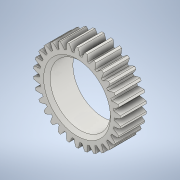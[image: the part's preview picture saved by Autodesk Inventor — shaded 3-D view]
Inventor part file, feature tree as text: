
AUTODESK INVENTOR PART (.ipt)
format: ipt  version: 2022 (Build 260153000, 153)  size: 621,568 bytes
history: native  units: mm (DEFAULTED — no unit token found)
features: plane x4, other x3, sketch x3, extrude x2, chamfer x1
ambient origin geometry x8: Origin, YZ Plane, XZ Plane, XY Plane, X Axis, Y Axis, Z Axis, Center Point
bodies: Solid1 (feature_tree)
feature tree (13):
  extrude  "Extrusion1"  Depth=9.525mm TaperAngle=0.0deg
  plane  "Work Plane1"
  plane  "Work Plane2"
  plane  "Work Plane3"
  other  "Spur Gear"
  extrude  "Extrusion2"  Depth=76.2mm TaperAngle=0.0deg
  plane  "Work Plane4"
  chamfer  "Chamfer1"  Distance=1.047198mm
  sketch  "Sketch1"  dims[d0=31.912126mm d1=9.525mm d2=0.0mm]
  sketch  "Sketch2"  dims[d3=30.0mm d4=76.2mm d5=0.0mm d6=0.0mm d7=1.047198mm]
  other  "Srf1"
  sketch  "Sketch3"  dims[d9=0.0mm d14=0.0mm d15=25.4mm d16=0.0mm d17=0.0mm d18=0.0mm d19=25.4mm d20=22.1mm d21=0.0mm d22=0.0mm d26=1.2mm d27=3.175mm d28=45.0deg]
  other  "Pitch Diameter"
